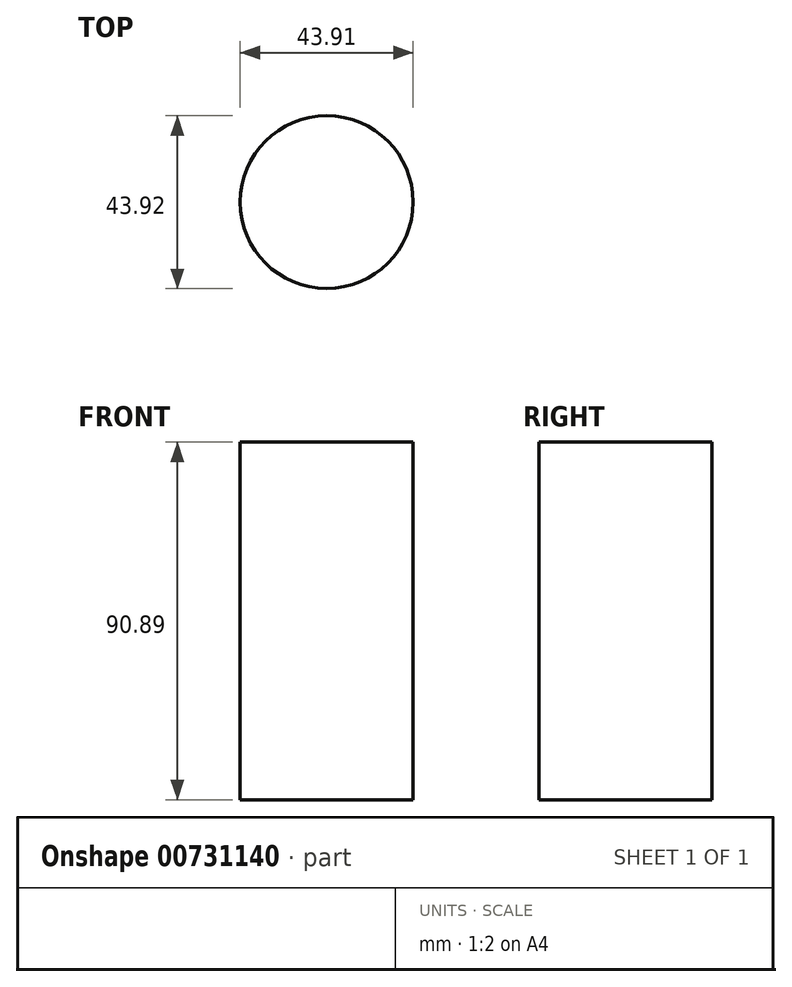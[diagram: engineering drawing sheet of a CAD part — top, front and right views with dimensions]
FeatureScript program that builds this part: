
annotation { "Feature Type Name" : "Feature", "Feature Type Description" : "" }
export const myFeature = defineFeature(function(context is Context, id is Id, definition is map)
    precondition{}
    {
        {
            var Q0;
            Q0=qCreatedBy(makeId("Top.planeOp"),FACE);
            var sketch = newSketch(context, id + "F0", { "sketchPlane" : qUnion([Q0])});
            skCircle(sketch, "E0", {"center": v(29.09, 24.26) * mm, "radius": 21.96 * mm});
            skSolve(sketch);
        }
        {
            var Q0;
            Q0 = qSketchRegion(id + "F0", true);
            extrude(context, id + "F1", {"entities" : qUnion([Q0]), "depth" : 90.9 * mm, "offsetDistance" : 25.4 * mm});
        }
    });
